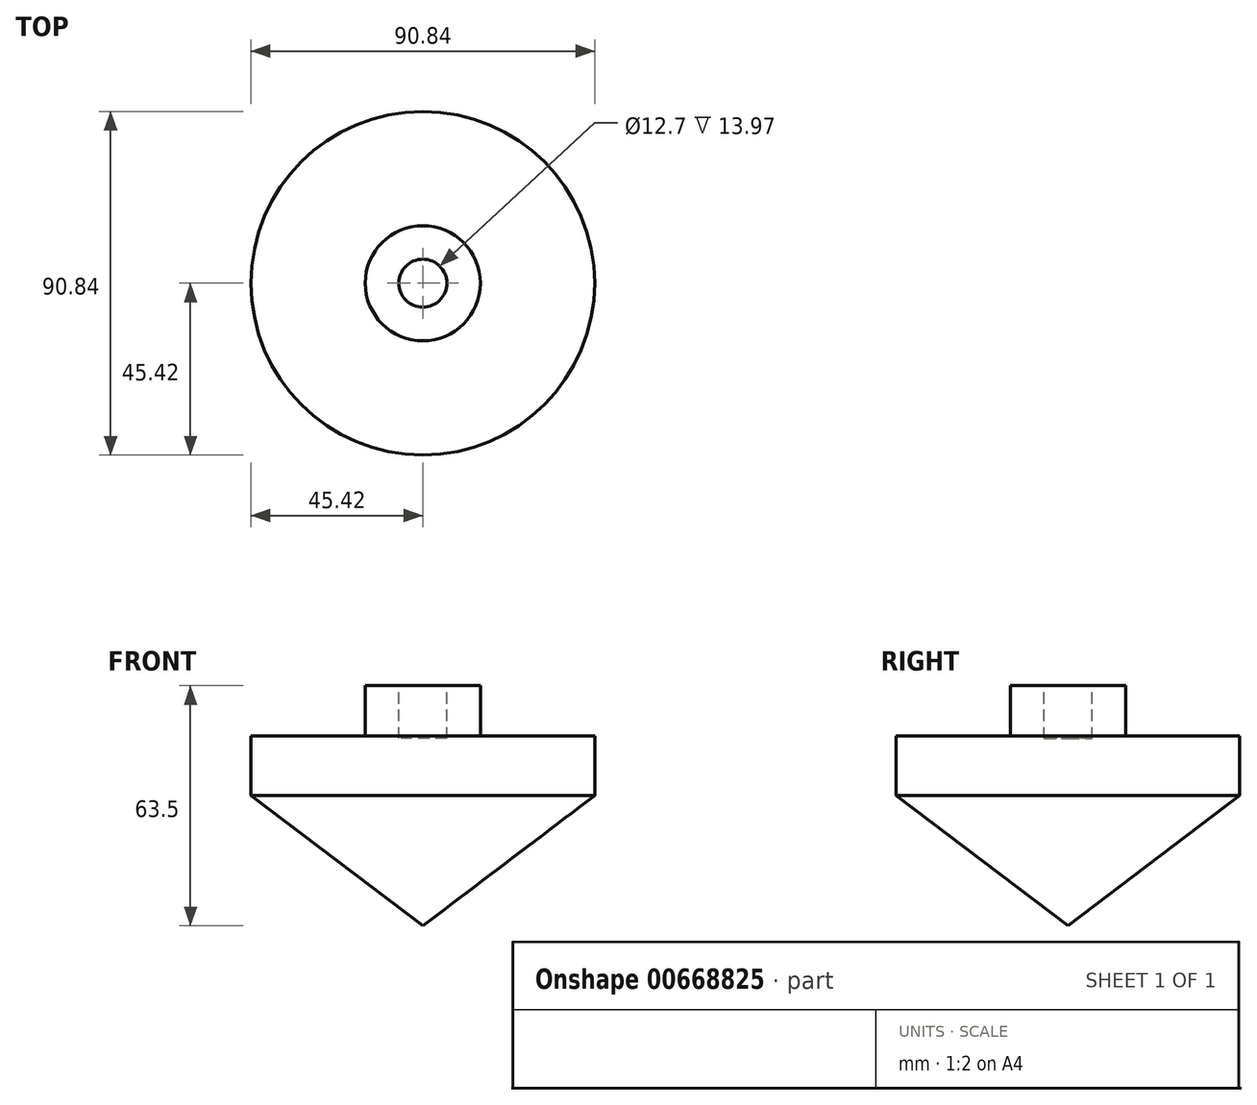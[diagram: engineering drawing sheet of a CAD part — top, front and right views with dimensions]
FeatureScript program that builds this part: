
annotation { "Feature Type Name" : "Feature", "Feature Type Description" : "" }
export const myFeature = defineFeature(function(context is Context, id is Id, definition is map)
    precondition{}
    {
        {
            var Q0;
            Q0=qCreatedBy(makeId("Front.planeOp"),FACE);
            var sketch = newSketch(context, id + "F0", { "sketchPlane" : qUnion([Q0])});
            skLineSegment(sketch, "E0", {"start": v(0, 0) * mm, "end": v(45.42, 34.42) * mm});
            skLineSegment(sketch, "E1", {"start": v(45.42, 34.42) * mm, "end": v(45.42, 50.2) * mm});
            skLineSegment(sketch, "E2", {"start": v(45.42, 50.2) * mm, "end": v(15.21, 50.2) * mm});
            skLineSegment(sketch, "E3", {"start": v(15.21, 50.2) * mm, "end": v(15.21, 63.5) * mm});
            skLineSegment(sketch, "E4", {"start": v(15.21, 63.5) * mm, "end": v(0, 63.5) * mm});
            skLineSegment(sketch, "E5", {"start": v(0, 63.5) * mm, "end": v(0, 0) * mm});
            skSolve(sketch);
        }
        {
            var Q0;
            Q0 = qSketchRegion(id + "F0", true);
            var Q1;
            Q1=sQuery(id+"F0.wireOp",EDGE,"E5");
            revolve(context, id + "F1", {"entities" : qUnion([Q0]), "axis" : qUnion([Q1]), "revolveType" : RevolveType.FULL});
        }
        {
            var Q0;
            Q0=makeQuery(id+"F1.opRevolve","SWEPT_FACE",FACE,{"disambiguationData":[OSD([sQuery(id+"F0.wireOp",EDGE,"E4")])]});
            var sketch = newSketch(context, id + "F2", { "sketchPlane" : qUnion([Q0])});
            skCircle(sketch, "E6", {"center": v(0, 0) * mm, "radius": 6.35 * mm});
            skSolve(sketch);
        }
        {
            var Q0;
            Q0 = qSketchRegion(id + "F2", true);
            extrude(context, id + "F3", {"entities" : qUnion([Q0]), "operationType" : NewBodyOperationType.REMOVE, "oppositeDirection" : true, "depth" : 13.97 * mm, "offsetDistance" : 25.4 * mm});
        }
    });
